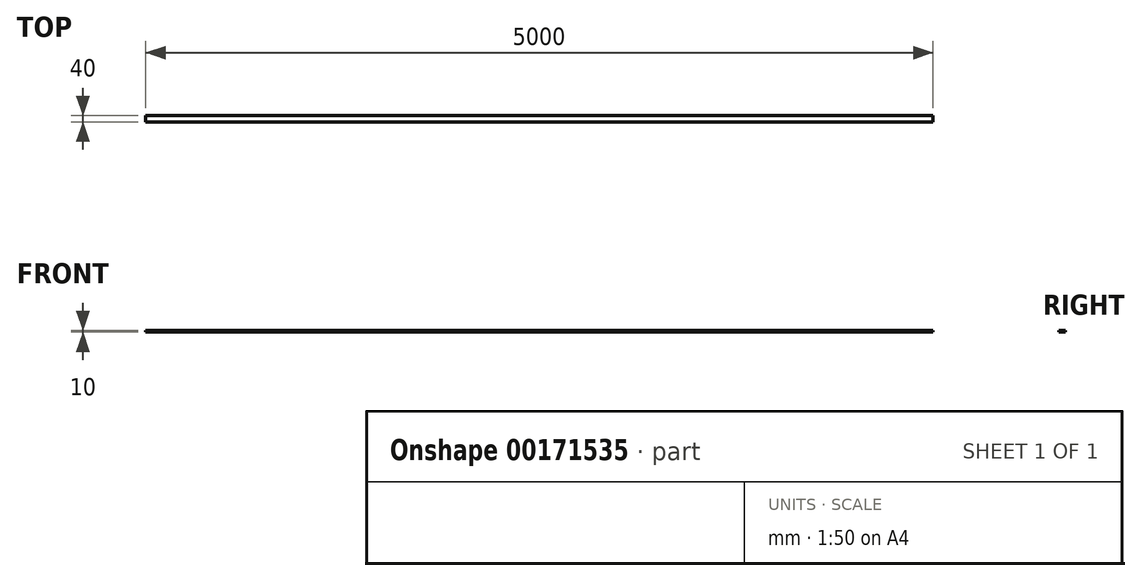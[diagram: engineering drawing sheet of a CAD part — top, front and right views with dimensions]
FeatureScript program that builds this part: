
annotation { "Feature Type Name" : "Feature", "Feature Type Description" : "" }
export const myFeature = defineFeature(function(context is Context, id is Id, definition is map)
    precondition{}
    {
        {
            var Q0;
            Q0=qCreatedBy(makeId("Top.planeOp"),FACE);
            var sketch = newSketch(context, id + "F0", { "sketchPlane" : qUnion([Q0])});
            skLineSegment(sketch, "E0.bottom", {"start": v(-2500, 20) * mm, "end": v(2500, 20) * mm});
            skLineSegment(sketch, "E0.top", {"start": v(-2500, -20) * mm, "end": v(2500, -20) * mm});
            skLineSegment(sketch, "E0.left", {"start": v(-2500, 20) * mm, "end": v(-2500, -20) * mm});
            skLineSegment(sketch, "E0.right", {"start": v(2500, 20) * mm, "end": v(2500, -20) * mm});
            skPoint(sketch, "E0.middle", {"position": v(0, 0) * mm});
            skSolve(sketch);
        }
        {
            var Q0;
            Q0=makeQuery(id+"F0.imprint","IMPRINT",FACE,{"disambiguationData":[TD([[makeQuery(id+"F0.imprint","IMPRINT",EDGE,{"derivedFrom":sQuery(id+"F0.wireOp",EDGE,"E0.bottom")}),-1.0]])]});
            extrude(context, id + "F1", {"entities" : qUnion([Q0]), "depth" : 10 * mm});
        }
    });
